# Revit family: Zahnplatte S
name_source: partatom
category: HLS-Bauteile
revit_build: Autodesk Revit 2017 (Build: 20190507_1515(x64)
units: mm (PartAtom-declared; Revit-internal decimal feet)

## family parameters
Arbeitsebenenbasiert = Ja
Beim Laden mit Abzugskörper schneiden = Nein
Bemaßung runder Anschluss = Durchmesser verwenden
Gemeinsam genutzt = Ja
Immer vertikal = Nein
Raumberechnungspunkt = Nein
Teiletyp = Normal

## types (3) — shared parameters
Abmessung = 36 x 20 x 8 mm
Anzugsmoment = 0.00 kN-m
B = 38 mm  [stored 0.124672 ft]
Breite = 20 mm  [stored 0.0656168 ft]
Fabrikat = MEFA
Firma = MEFA Befestigungs- und Montagesysteme GmbH
Form = einschwenkbar
Gewicht = 0.06 kg
Gewicht pro Bauteil = 0.06 kg
Kurztext1 = Zahnplatte S
Länge = 36 mm  [stored 0.11811 ft]
Material = Stahl
Mengeneinheit = St
Oberflaeche = galvanisch verzinkt
Profil = C-Profil
Profiltyp = 45
S = 12 mm  [stored 0.0393701 ft]
Schienenbreite = 45 mm
Stärke Material = 8 mm  [stored 0.0262467 ft]
Vorgabe-Ansicht = 1219 mm
vpe = 100 St

## per-type parameters (varying)
| type | Artikelnummer | EAN | Gewinde | Kurztext2 | d2 |
| Zahnplatte S M10 | 0818102 | 4250928420572 | M10 | M10 36 x 20 mm gvz | 4 mm  [stored 0.0131234 ft] |
| Zahnplatte S M 8 | 0818101 | 4250928449108 | M8 | M8 36 x 20 mm gvz | 3 mm  [stored 0.00984252 ft] |
| Zahnplatte S M12 | 0818103 | 4250928449122 | M12 | M12 36 x 20 mm gvz | 5 mm  [stored 0.0164042 ft] |

note: [stored X ft] marks values corroborated as IEEE doubles in the binary element streams (Revit-internal decimal feet)
